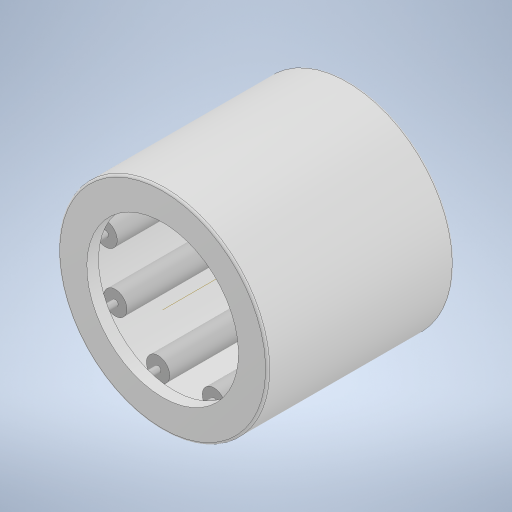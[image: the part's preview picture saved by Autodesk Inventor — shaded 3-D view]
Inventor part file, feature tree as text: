
AUTODESK INVENTOR PART (.ipt)
format: ipt  version: 2023.2 (Build 272271000, 271)  size: 313,856 bytes
history: mixed  units: in
note: dims shown in document units (in); Inventor stores cm internally (conversion verified against a paired STEP export)
features: other x17, revolve x2, fillet x1, imported_body x1
ambient origin geometry x8: Origin, YZ Plane, XZ Plane, XY Plane, X Axis, Y Axis, Z Axis, Center Point
bodies: Solid1 (imported_parasolid), Solid2 (imported_parasolid), Solid3 (imported_parasolid), Solid4 (imported_parasolid), Solid5 (imported_parasolid), Solid6 (imported_parasolid), Solid7 (imported_parasolid), Solid8 (imported_parasolid), Solid9 (imported_parasolid), Solid10 (imported_parasolid), Solid11 (imported_parasolid), Solid12 (imported_parasolid), Solid13 (imported_parasolid), Solid14 (imported_parasolid), Solid15 (imported_parasolid), Solid16 (imported_parasolid), Solid17 (imported_parasolid), Solid18 (imported_parasolid), Solid19 (imported_parasolid)
feature tree (21):
  other  "Axis1"
  revolve  "Revolve2"  [1 undecoded]
  revolve  "Revolve3"  [1 undecoded]
  other  "CirPattern1[1]"
  other  "CirPattern1[2]"
  other  "CirPattern1[3]"
  other  "CirPattern1[4]"
  other  "CirPattern1[5]"
  other  "CirPattern1[6]"
  other  "CirPattern1[7]"
  other  "CirPattern1[8]"
  other  "CirPattern1[9]"
  other  "CirPattern1[10]"
  other  "CirPattern1[11]"
  other  "CirPattern1[12]"
  other  "CirPattern1[13]"
  other  "CirPattern1[14]"
  other  "CirPattern1[15]"
  other  "CirPattern1[16]"
  fillet  "Fillet1"  [1 undecoded]
  imported_body  NMx_Import_Brep_tag  [imported B-rep: ~73 faces, bbox_mm=[11.047051, 14.2875, 12.7]]
note: 3 required parameter values undecoded (feature->parameter linkage not recoverable at this tier; creation-order binding heuristic only, values carry confidence <= 0.55)
